# Revit family: LEGRAND_PRISES_NON_VERROUILLEES_SAILLIES_IP66_230
name_source: partatom
category: Installations électriques
revit_build: Autodesk Revit 2018 (Build: 20170223_1515(x64)
units: mm (PartAtom-declared; Revit-internal decimal feet)

## family parameters
Conserver l'orientation des annotations = Non
Cote de connecteur circulaire = Utiliser le diamètre
Couper avec des vides une fois chargée = Non
Hôte = Face
Partagée = Non
Point de calcul de pièce = Non
Type d'élément = Normal

## types (10) — shared parameters
Conditions Générale d'Utilisation = https://export.legrand.com
Couleur caractéristique = bleu
Description = Prise au standard international pour montage encastré ou saillie avec accessoire permet la connexion d'appareils de puissance
Dia bouchon = 90 mm  [stored 0.295276 ft]
Elévation par défaut = 1000 mm  [stored 3.28084 ft]
Fabricant = Legrand
L2 = 45 mm  [stored 0.147638 ft]
RAY BOUCHON = 45 mm  [stored 0.147638 ft]
Ray = 28 mm
Standard CEI ou NFC = CEI
Température maximale d'installation = 40°C
Température maximum d'utilisation = 100°C
Température minimum d'installation = -20°C
Température minimum d'utilisation = -50°C
Tension V = 230 V  50/60 Hz  bleu
classe de protection IP = IP66/67-55
dIA = 56 mm
installation Encastrée E ou Saillie S = encastré et saillie
matériau du boitier = plastique
résistance aux chocs IK = 09
sans halogène = Non
type de raccordement = bornes à vis

## per-type parameters (varying)
| type | Intensité A | Modèle | Nombre de pôles | Position de la Terre h | entraxe de fixation horizontal mm | entraxe de fixation vertical mm | h1 | hauteur mm | largeur mm | profondeur d'encastrement mm | profondeur mm |
| Socle tableau Hypra   IP66/67-55   16 A   200/250 V   2P+T   plast saillie boitier simple | 16 A | 051126 | 3 | 6 | 52 mm | 60 mm | 64 mm | 106 mm | 74 mm | 58 mm | 115 mm |
| Socle tableau Hypra   IP66/67-55   16 A   200/250 V   3P T   plast saillie boitier simple | 16 A | 051127 | 6 | 6 | 60 mm | 70 mm | 64 mm | 106 mm | 74 mm | 58 mm | 106 mm |
| Socle tableau entraxe unifié Hypra  IP66/67-55  32 A   200/250 V   2P+T   plast saillie boitier passage | 32 A | 053046 | 3 | 6 | 70 mm | 70 mm | 97 mm | 162 mm | 102 mm | 90 mm  [stored 0.295276 ft] | 150 mm |
| Socle tableau entraxe unifié Hypra  IP66/67-55  32 A   230 V   3P+T   plast saillie boitier passage | 32 A | 053047 | 4 | 9 | 70 mm | 70 mm | 97 mm | 162 mm | 102 mm | 90 mm  [stored 0.295276 ft] | 160 mm  [stored 0.524934 ft] |
| Socle de tableau Hypra  IP 66/67-55   63A   200/250 V   2P+T   plast saillie boitier passage | 63 A | 059326 | 3 | 6 | 77 mm | 85 mm | 180 mm  [stored 0.590551 ft] | 300 mm | 170 mm | 150 mm | 215 mm |
| Socle tableau Hypra  IP IP 66/67-55  63 A    230 V   3P+T plast saillie boitier passage | 63 A | 059327 | 4 | 9 | 77 mm | 85 mm | 180 mm  [stored 0.590551 ft] | 300 mm | 170 mm | 150 mm | 255 mm  [stored 0.836614 ft] |
| Socle tableau Hypra   IP 66/67-55   16 A   200/250 V   2P+T   plast saillie boitier passage | 16 A | 051126 | 3 | 6 | 52 mm | 60 mm | 109 mm | 182 mm | 86 mm | 75 mm | 135 mm  [stored 0.442913 ft] |
| Socle tableau Hypra   IP 66/67-55   16 A   200/250 V   3P+T   plas saillie boitier passage | 16 A | 051127 | 6 | 6 | 60 mm | 70 mm | 109 mm | 182 mm | 86 mm | 75 mm | 135 mm  [stored 0.442913 ft] |
| Socle tableau entraxe unifié Hypra  IP66/67-55  32 A   200/250 V   2P+T   plast saillie boitier simple | 32 A | 053046 | 3 | 6 | 70 mm | 70 mm | 97 mm | 162 mm | 102 mm | 90 mm  [stored 0.295276 ft] | 160 mm  [stored 0.524934 ft] |
| Socle tableau entraxe unifié Hypra  IP66/67-55  32 A   230 V   3P+T   plast saillie boitier simple | 32 A | 053047 | 4 | 9 | 70 mm | 70 mm | 97 mm | 162 mm | 102 mm | 90 mm  [stored 0.295276 ft] | 160 mm  [stored 0.524934 ft] |

note: [stored X ft] marks values corroborated as IEEE doubles in the binary element streams (Revit-internal decimal feet)
